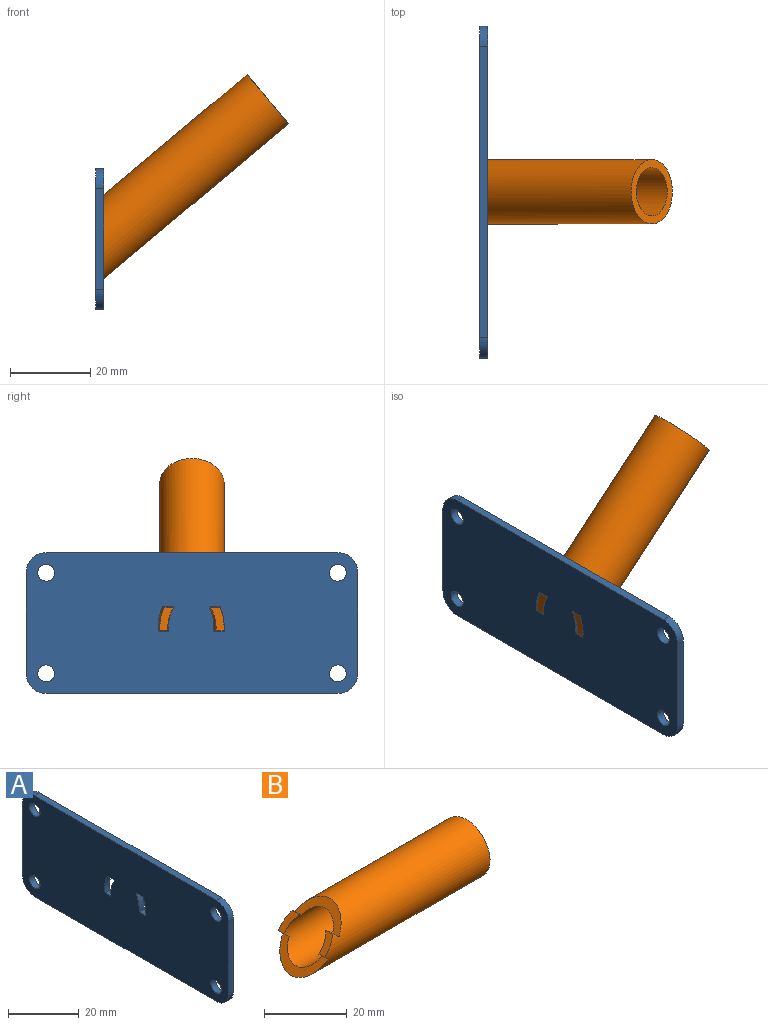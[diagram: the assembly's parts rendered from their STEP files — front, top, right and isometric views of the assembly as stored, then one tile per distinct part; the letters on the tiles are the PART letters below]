
ASSEMBLY  parts=2 mates=1
PART A: 22 faces, bbox 2x82.5x35 mm
  f0: plane 2.36x2mm, normal (0,-0.02,1), area 4.7mm2, adj f1,f19,f20,f21
  f1: extruded ~6.22x2mm, area 12.9mm2, adj f0,f2,f20,f21
  f2: plane 2.89x2mm, normal (0,-0.02,-1), area 5.8mm2, adj f1,f19,f20,f21
  f3: plane 2.69x2mm, normal (0,-0.02,-1), area 5.4mm2, adj f4,f13,f20,f21
  f4: extruded ~6x2mm, area 12.4mm2, adj f3,f5,f20,f21
  f5: plane 2.53x2mm, normal (0,-0.03,1), area 5.1mm2, adj f4,f13,f20,f21
  f6: plane 72.5x2mm, normal (0,0,1), area 145mm2, adj f7,f14,f20,f21
  f7: cylinder r=5mm len=5mm, axis (-1,0,0), area 15.7mm2, adj f6,f8,f20,f21
  f8: plane 25x2mm, normal (0,-1,0), area 50mm2, adj f7,f9,f20,f21
  f9: cylinder r=5mm len=5mm, axis (-1,0,0), area 15.7mm2, adj f8,f10,f20,f21
  f10: plane 72.5x2mm, normal (0,0,-1), area 145mm2, adj f9,f11,f20,f21
  f11: cylinder r=5mm len=5mm, axis (-1,0,0), area 15.7mm2, adj f10,f12,f20,f21
  f12: plane 25x2mm, normal (0,1,0), area 50mm2, adj f11,f14,f20,f21
  f13: extruded ~6.15x2mm, area 12.6mm2, adj f3,f5,f20,f21
  f14: cylinder r=5mm len=5mm, axis (-1,0,0), area 15.7mm2, adj f6,f12,f20,f21
  f15: cylinder r=2.1mm len=4.2mm, axis (-1,0,0), area 26.4mm2, adj f20,f21
  f16: cylinder r=2.1mm len=4.2mm, axis (-1,0,0), area 26.4mm2, adj f20,f21
  f17: cylinder r=2.1mm len=4.2mm, axis (-1,0,0), area 26.4mm2, adj f20,f21
  f18: cylinder r=2.1mm len=4.2mm, axis (-1,0,0), area 26.4mm2, adj f20,f21
  f19: extruded ~6.13x2mm, area 12.5mm2, adj f0,f2,f20,f21
  f20: plane 82.5x35mm, normal (1,0,0), area 2778.9mm2, adj f0,f1,f2,f3,f4,f5,f6,f7
  f21: plane 82.5x35mm, normal (-1,0,0), area 2778.9mm2, adj f0,f1,f2,f3,f4,f5,f6,f7
PART B: 11 faces, bbox 60x16x16 mm
  f0: cylinder r=6mm len=58.33mm, axis (-1,0,0), area 2033.6mm2, adj f2,f3,f4,f5,f6,f7,f8,f9
  f1: cylinder r=8mm len=60.02mm, axis (-1,0,0), area 2702.7mm2, adj f2,f3,f4,f5,f6,f7,f8,f9
  f2: plane 16x16mm, normal (1,0,0), area 88mm2, adj f0,f1
  f3: plane 15.13x5.38mm, normal (-0.77,0,0.64), area 43.3mm2, adj f0,f1,f9,f10
  f4: plane 15.56x6.13mm, normal (-0.77,0,0.64), area 47.5mm2, adj f0,f1,f5,f6
  f5: plane 2.3x1.55mm, normal (-0.64,0,-0.77), area 4.1mm2, adj f0,f1,f4,f8
  f6: plane 2.3x1.55mm, normal (-0.64,0,-0.77), area 4.1mm2, adj f0,f1,f4,f7
  f7: plane 4.51x3.78mm, normal (-0.77,0,0.64), area 12.4mm2, adj f0,f1,f6,f10
  f8: plane 4.51x3.78mm, normal (-0.77,0,0.64), area 12.4mm2, adj f0,f1,f5,f9
  f9: plane 3.04x1.56mm, normal (0.64,0,0.77), area 4.6mm2, adj f0,f1,f3,f8
  f10: plane 3.04x1.56mm, normal (0.64,0,0.77), area 4.6mm2, adj f0,f1,f3,f7
PLACE A t=(-46.95,-11.96,72.4)mm
PLACE B rot(axis=(0,-1,0),40deg) t=(-50.09,-53.19,68.62)mm
MATE fastened B.f7 <-> A.f21  axis (-1,0,0) through (-46.95,-46.56,73.53)mm
